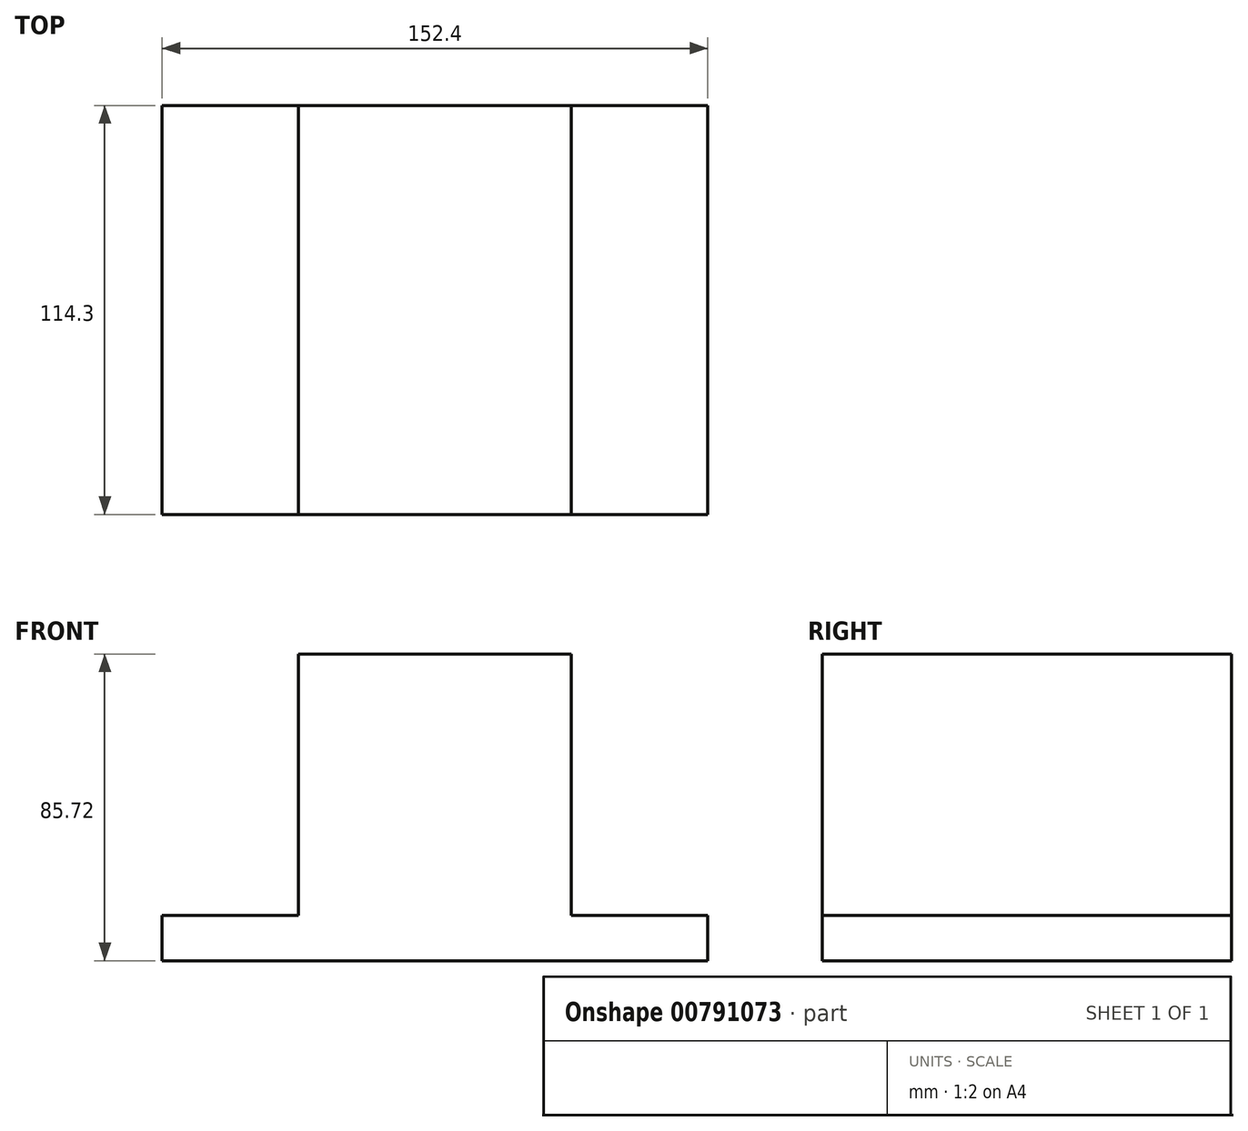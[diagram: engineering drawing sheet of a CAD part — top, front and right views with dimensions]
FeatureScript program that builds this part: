
annotation { "Feature Type Name" : "Feature", "Feature Type Description" : "" }
export const myFeature = defineFeature(function(context is Context, id is Id, definition is map)
    precondition{}
    {
        {
            var Q0;
            Q0=qCreatedBy(makeId("Front.planeOp"),FACE);
            var sketch = newSketch(context, id + "F0", { "sketchPlane" : qUnion([Q0])});
            skLineSegment(sketch, "E0", {"start": v(0, 0) * mm, "end": v(152.4, 0) * mm});
            skLineSegment(sketch, "E1", {"start": v(152.4, 0) * mm, "end": v(152.4, 12.7) * mm});
            skLineSegment(sketch, "E2", {"start": v(152.4, 12.7) * mm, "end": v(114.3, 12.7) * mm});
            skLineSegment(sketch, "E3", {"start": v(114.3, 12.7) * mm, "end": v(114.3, 85.72) * mm});
            skLineSegment(sketch, "E4", {"start": v(114.3, 85.72) * mm, "end": v(38.1, 85.72) * mm});
            skLineSegment(sketch, "E5", {"start": v(38.1, 85.72) * mm, "end": v(38.1, 12.7) * mm});
            skLineSegment(sketch, "E6", {"start": v(38.1, 12.7) * mm, "end": v(0, 12.7) * mm});
            skLineSegment(sketch, "E7", {"start": v(0, 12.7) * mm, "end": v(0, 0) * mm});
            skSolve(sketch);
        }
        {
            var Q0;
            Q0 = qSketchRegion(id + "F0", true);
            extrude(context, id + "F1", {"entities" : qUnion([Q0]), "depth" : 114.3 * mm, "offsetDistance" : 25.4 * mm});
        }
    });
